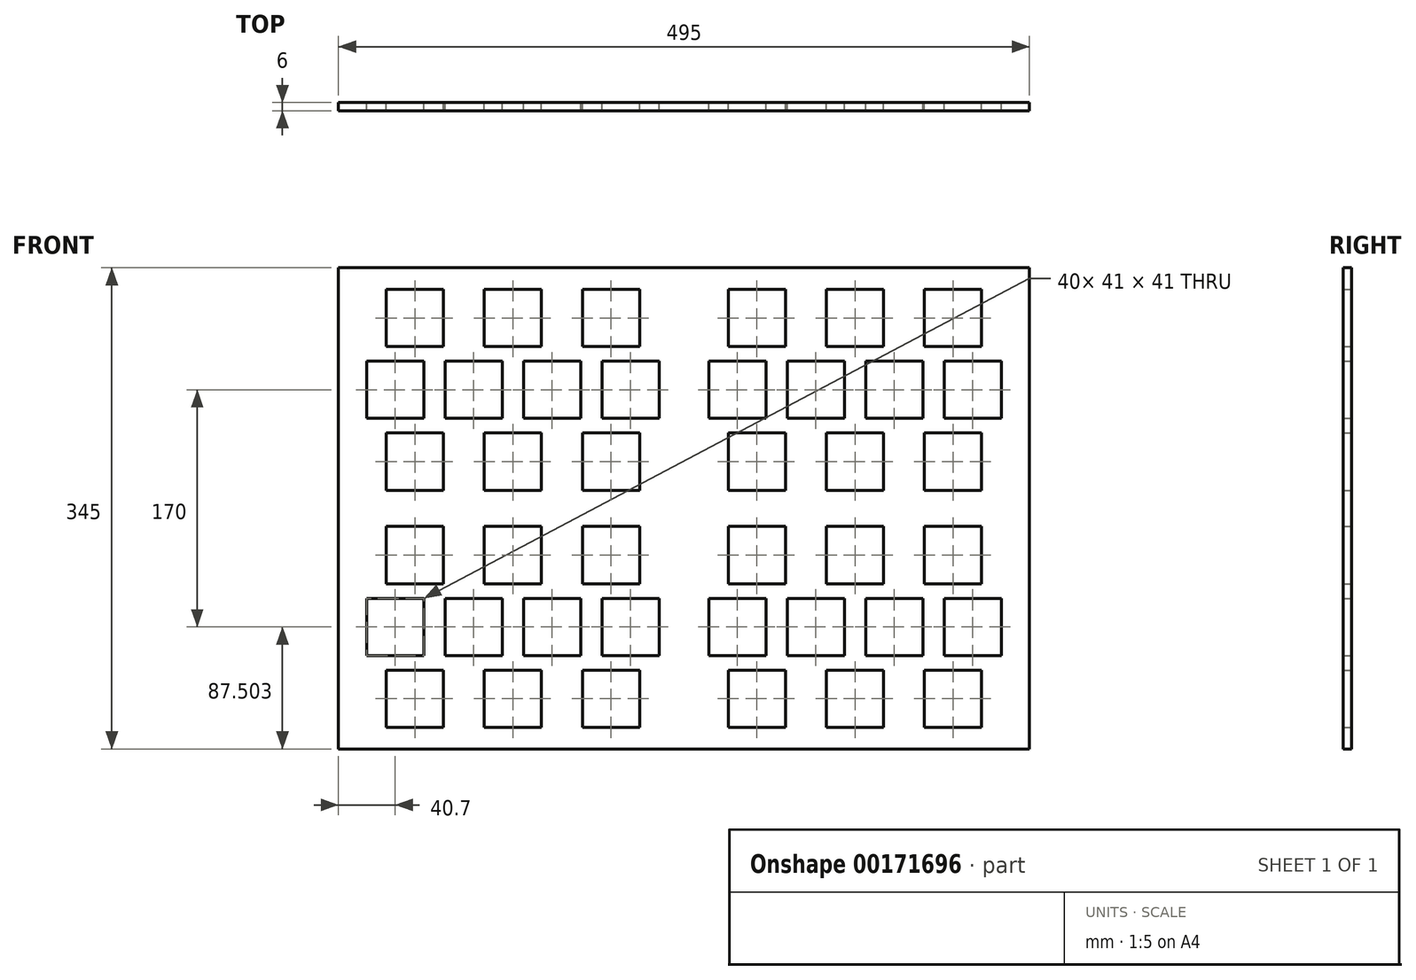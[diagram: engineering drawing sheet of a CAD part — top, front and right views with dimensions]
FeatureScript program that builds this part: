
annotation { "Feature Type Name" : "Feature", "Feature Type Description" : "" }
export const myFeature = defineFeature(function(context is Context, id is Id, definition is map)
    precondition{}
    {
        {
            var Q0;
            Q0=qCreatedBy(makeId("Front.planeOp"),FACE);
            var sketch = newSketch(context, id + "F0", { "sketchPlane" : qUnion([Q0])});
            skLineSegment(sketch, "E0.bottom", {"start": v(228.25, -174.12) * mm, "end": v(-226.75, -174.12) * mm});
            skLineSegment(sketch, "E0.top", {"start": v(227.5, 170.88) * mm, "end": v(-227.5, 170.88) * mm});
            skLineSegment(sketch, "E0.left", {"start": v(248.25, -154.12) * mm, "end": v(248.25, 150.88) * mm});
            skLineSegment(sketch, "E0.right", {"start": v(-246.75, -152.5) * mm, "end": v(-246.75, 152.5) * mm});
            skPoint(sketch, "E1.visualSharp", {"position": v(-246.75, 170.88) * mm});
            skPoint(sketch, "E2.visualSharp", {"position": v(248.25, -174.12) * mm});
            skPoint(sketch, "E3.visualSharp", {"position": v(-246.75, -174.12) * mm});
            skLineSegment(sketch, "E4", {"start": v(-246.75, 152.5) * mm, "end": v(-246.75, 170.88) * mm});
            skLineSegment(sketch, "E5", {"start": v(-246.75, 170.88) * mm, "end": v(-227.5, 170.88) * mm});
            skLineSegment(sketch, "E6", {"start": v(-246.75, -174.12) * mm, "end": v(-246.75, -152.5) * mm});
            skLineSegment(sketch, "E7", {"start": v(-246.75, -174.12) * mm, "end": v(-226.75, -174.12) * mm});
            skLineSegment(sketch, "E8", {"start": v(248.25, -154.12) * mm, "end": v(248.25, -174.12) * mm});
            skLineSegment(sketch, "E9", {"start": v(228.25, -174.12) * mm, "end": v(248.25, -174.12) * mm});
            skLineSegment(sketch, "E10", {"start": v(227.5, 170.88) * mm, "end": v(248.25, 170.88) * mm});
            skLineSegment(sketch, "E11", {"start": v(248.25, 150.88) * mm, "end": v(248.25, 170.88) * mm});
            skPoint(sketch, "E12.0.1.2", {"position": v(-247.5, 2.5) * mm});
            skLineSegment(sketch, "E13.bottom", {"start": v(-212.5, 155.38) * mm, "end": v(-171.5, 155.38) * mm});
            skLineSegment(sketch, "E13.top", {"start": v(-212.5, 114.38) * mm, "end": v(-171.5, 114.38) * mm});
            skLineSegment(sketch, "E13.left", {"start": v(-212.5, 155.38) * mm, "end": v(-212.5, 114.38) * mm});
            skLineSegment(sketch, "E13.right", {"start": v(-171.5, 155.38) * mm, "end": v(-171.5, 114.38) * mm});
            skLineSegment(sketch, "E14.0.1.0", {"start": v(-212.5, 52.38) * mm, "end": v(-171.5, 52.38) * mm});
            skLineSegment(sketch, "E14.0.1.1", {"start": v(-212.5, 11.38) * mm, "end": v(-171.5, 11.38) * mm});
            skLineSegment(sketch, "E14.0.1.2", {"start": v(-171.5, 52.38) * mm, "end": v(-171.5, 11.38) * mm});
            skLineSegment(sketch, "E14.0.1.3", {"start": v(-212.5, 52.38) * mm, "end": v(-212.5, 11.38) * mm});
            skLineSegment(sketch, "E14.1.0.0", {"start": v(-142.25, 155.38) * mm, "end": v(-101.25, 155.38) * mm});
            skLineSegment(sketch, "E14.1.0.1", {"start": v(-142.25, 114.38) * mm, "end": v(-101.25, 114.38) * mm});
            skLineSegment(sketch, "E14.1.0.2", {"start": v(-101.25, 155.38) * mm, "end": v(-101.25, 114.38) * mm});
            skLineSegment(sketch, "E14.1.0.3", {"start": v(-142.25, 155.38) * mm, "end": v(-142.25, 114.38) * mm});
            skLineSegment(sketch, "E14.1.1.0", {"start": v(-142.25, 52.38) * mm, "end": v(-101.25, 52.38) * mm});
            skLineSegment(sketch, "E14.1.1.1", {"start": v(-142.25, 11.38) * mm, "end": v(-101.25, 11.38) * mm});
            skLineSegment(sketch, "E14.1.1.2", {"start": v(-101.25, 52.38) * mm, "end": v(-101.25, 11.38) * mm});
            skLineSegment(sketch, "E14.1.1.3", {"start": v(-142.25, 52.38) * mm, "end": v(-142.25, 11.38) * mm});
            skLineSegment(sketch, "E14.2.0.0", {"start": v(-72, 155.38) * mm, "end": v(-31, 155.38) * mm});
            skLineSegment(sketch, "E14.2.0.1", {"start": v(-72, 114.38) * mm, "end": v(-31, 114.38) * mm});
            skLineSegment(sketch, "E14.2.0.2", {"start": v(-31, 155.38) * mm, "end": v(-31, 114.38) * mm});
            skLineSegment(sketch, "E14.2.0.3", {"start": v(-72, 155.38) * mm, "end": v(-72, 114.38) * mm});
            skLineSegment(sketch, "E14.2.1.0", {"start": v(-72, 52.38) * mm, "end": v(-31, 52.38) * mm});
            skLineSegment(sketch, "E14.2.1.1", {"start": v(-72, 11.38) * mm, "end": v(-31, 11.38) * mm});
            skLineSegment(sketch, "E14.2.1.2", {"start": v(-31, 52.38) * mm, "end": v(-31, 11.38) * mm});
            skLineSegment(sketch, "E14.2.1.3", {"start": v(-72, 52.38) * mm, "end": v(-72, 11.38) * mm});
            skLineSegment(sketch, "E14.direction1", {"start": v(-212.5, 114.38) * mm, "end": v(-142.25, 114.38) * mm, "construction": true});
            skLineSegment(sketch, "E14.direction2", {"start": v(-212.5, 114.38) * mm, "end": v(-212.5, 11.38) * mm, "construction": true});
            skLineSegment(sketch, "E15.bottom", {"start": v(-226.55, 103.88) * mm, "end": v(-185.55, 103.88) * mm});
            skLineSegment(sketch, "E15.top", {"start": v(-226.55, 62.88) * mm, "end": v(-185.55, 62.88) * mm});
            skLineSegment(sketch, "E15.left", {"start": v(-226.55, 103.88) * mm, "end": v(-226.55, 62.88) * mm});
            skLineSegment(sketch, "E15.right", {"start": v(-185.55, 103.88) * mm, "end": v(-185.55, 62.88) * mm});
            skLineSegment(sketch, "E16.1.0.0", {"start": v(-170.35, 103.88) * mm, "end": v(-129.35, 103.88) * mm});
            skLineSegment(sketch, "E16.1.0.1", {"start": v(-129.35, 103.88) * mm, "end": v(-129.35, 62.88) * mm});
            skLineSegment(sketch, "E16.1.0.2", {"start": v(-170.35, 103.88) * mm, "end": v(-170.35, 62.88) * mm});
            skLineSegment(sketch, "E16.1.0.3", {"start": v(-170.35, 62.88) * mm, "end": v(-129.35, 62.88) * mm});
            skLineSegment(sketch, "E16.2.0.0", {"start": v(-114.15, 103.88) * mm, "end": v(-73.15, 103.88) * mm});
            skLineSegment(sketch, "E16.2.0.1", {"start": v(-73.15, 103.88) * mm, "end": v(-73.15, 62.88) * mm});
            skLineSegment(sketch, "E16.2.0.2", {"start": v(-114.15, 103.88) * mm, "end": v(-114.15, 62.88) * mm});
            skLineSegment(sketch, "E16.2.0.3", {"start": v(-114.15, 62.88) * mm, "end": v(-73.15, 62.88) * mm});
            skLineSegment(sketch, "E16.3.0.0", {"start": v(-57.95, 103.88) * mm, "end": v(-16.95, 103.88) * mm});
            skLineSegment(sketch, "E16.3.0.1", {"start": v(-16.95, 103.88) * mm, "end": v(-16.95, 62.88) * mm});
            skLineSegment(sketch, "E16.3.0.2", {"start": v(-57.95, 103.88) * mm, "end": v(-57.95, 62.88) * mm});
            skLineSegment(sketch, "E16.3.0.3", {"start": v(-57.95, 62.88) * mm, "end": v(-16.95, 62.88) * mm});
            skLineSegment(sketch, "E16.direction1", {"start": v(-226.55, 62.88) * mm, "end": v(-170.35, 62.88) * mm, "construction": true});
            skLineSegment(sketch, "E17.0.1.0", {"start": v(-57.95, -107.12) * mm, "end": v(-16.95, -107.12) * mm});
            skLineSegment(sketch, "E17.0.1.1", {"start": v(-72, -14.62) * mm, "end": v(-72, -55.62) * mm});
            skLineSegment(sketch, "E17.0.1.2", {"start": v(-226.55, -66.12) * mm, "end": v(-226.55, -107.12) * mm});
            skLineSegment(sketch, "E17.0.1.3", {"start": v(-185.55, -66.12) * mm, "end": v(-185.55, -107.12) * mm});
            skLineSegment(sketch, "E17.0.1.4", {"start": v(-72, -55.62) * mm, "end": v(-31, -55.62) * mm});
            skLineSegment(sketch, "E17.0.1.5", {"start": v(-57.95, -66.12) * mm, "end": v(-57.95, -107.12) * mm});
            skLineSegment(sketch, "E17.0.1.6", {"start": v(-170.35, -66.12) * mm, "end": v(-129.35, -66.12) * mm});
            skLineSegment(sketch, "E17.0.1.7", {"start": v(-212.5, -117.62) * mm, "end": v(-171.5, -117.62) * mm});
            skLineSegment(sketch, "E17.0.1.8", {"start": v(-212.5, -158.62) * mm, "end": v(-171.5, -158.62) * mm});
            skLineSegment(sketch, "E17.0.1.9", {"start": v(-73.15, -66.12) * mm, "end": v(-73.15, -107.12) * mm});
            skLineSegment(sketch, "E17.0.1.10", {"start": v(-114.15, -66.12) * mm, "end": v(-114.15, -107.12) * mm});
            skLineSegment(sketch, "E17.0.1.11", {"start": v(-72, -117.62) * mm, "end": v(-31, -117.62) * mm});
            skLineSegment(sketch, "E17.0.1.12", {"start": v(-72, -158.62) * mm, "end": v(-31, -158.62) * mm});
            skLineSegment(sketch, "E17.0.1.13", {"start": v(-212.5, -14.62) * mm, "end": v(-171.5, -14.62) * mm});
            skLineSegment(sketch, "E17.0.1.14", {"start": v(-226.55, -107.12) * mm, "end": v(-170.35, -107.12) * mm, "construction": true});
            skLineSegment(sketch, "E17.0.1.15", {"start": v(-31, -117.62) * mm, "end": v(-31, -158.62) * mm});
            skLineSegment(sketch, "E17.0.1.16", {"start": v(-142.25, -117.62) * mm, "end": v(-142.25, -158.62) * mm});
            skLineSegment(sketch, "E17.0.1.17", {"start": v(-129.35, -66.12) * mm, "end": v(-129.35, -107.12) * mm});
            skLineSegment(sketch, "E17.0.1.18", {"start": v(-57.95, -66.12) * mm, "end": v(-16.95, -66.12) * mm});
            skLineSegment(sketch, "E17.0.1.19", {"start": v(-170.35, -66.12) * mm, "end": v(-170.35, -107.12) * mm});
            skLineSegment(sketch, "E17.0.1.20", {"start": v(-114.15, -107.12) * mm, "end": v(-73.15, -107.12) * mm});
            skLineSegment(sketch, "E17.0.1.21", {"start": v(-142.25, -55.62) * mm, "end": v(-101.25, -55.62) * mm});
            skLineSegment(sketch, "E17.0.1.22", {"start": v(-212.5, -55.62) * mm, "end": v(-212.5, -158.62) * mm, "construction": true});
            skLineSegment(sketch, "E17.0.1.23", {"start": v(-72, -14.62) * mm, "end": v(-31, -14.62) * mm});
            skLineSegment(sketch, "E17.0.1.24", {"start": v(-16.95, -66.12) * mm, "end": v(-16.95, -107.12) * mm});
            skLineSegment(sketch, "E17.0.1.25", {"start": v(-72, -117.62) * mm, "end": v(-72, -158.62) * mm});
            skLineSegment(sketch, "E17.0.1.26", {"start": v(-171.5, -14.62) * mm, "end": v(-171.5, -55.62) * mm});
            skLineSegment(sketch, "E17.0.1.27", {"start": v(-142.25, -117.62) * mm, "end": v(-101.25, -117.62) * mm});
            skLineSegment(sketch, "E17.0.1.28", {"start": v(-226.55, -66.12) * mm, "end": v(-185.55, -66.12) * mm});
            skLineSegment(sketch, "E17.0.1.29", {"start": v(-101.25, -117.62) * mm, "end": v(-101.25, -158.62) * mm});
            skLineSegment(sketch, "E17.0.1.30", {"start": v(-114.15, -66.12) * mm, "end": v(-73.15, -66.12) * mm});
            skLineSegment(sketch, "E17.0.1.31", {"start": v(-31, -14.62) * mm, "end": v(-31, -55.62) * mm});
            skLineSegment(sketch, "E17.0.1.32", {"start": v(-212.5, -14.62) * mm, "end": v(-212.5, -55.62) * mm});
            skLineSegment(sketch, "E17.0.1.33", {"start": v(-142.25, -158.62) * mm, "end": v(-101.25, -158.62) * mm});
            skLineSegment(sketch, "E17.0.1.34", {"start": v(-212.5, -55.62) * mm, "end": v(-142.25, -55.62) * mm, "construction": true});
            skLineSegment(sketch, "E17.0.1.35", {"start": v(-142.25, -14.62) * mm, "end": v(-142.25, -55.62) * mm});
            skLineSegment(sketch, "E17.0.1.36", {"start": v(-170.35, -107.12) * mm, "end": v(-129.35, -107.12) * mm});
            skLineSegment(sketch, "E17.0.1.37", {"start": v(-171.5, -117.62) * mm, "end": v(-171.5, -158.62) * mm});
            skLineSegment(sketch, "E17.0.1.38", {"start": v(-101.25, -14.62) * mm, "end": v(-101.25, -55.62) * mm});
            skLineSegment(sketch, "E17.0.1.39", {"start": v(-142.25, -14.62) * mm, "end": v(-101.25, -14.62) * mm});
            skLineSegment(sketch, "E17.0.1.40", {"start": v(-212.5, -55.62) * mm, "end": v(-171.5, -55.62) * mm});
            skLineSegment(sketch, "E17.0.1.41", {"start": v(-226.55, -107.12) * mm, "end": v(-185.55, -107.12) * mm});
            skLineSegment(sketch, "E17.0.1.42", {"start": v(-212.5, -117.62) * mm, "end": v(-212.5, -158.62) * mm});
            skLineSegment(sketch, "E17.1.0.0", {"start": v(187.05, 62.88) * mm, "end": v(228.05, 62.88) * mm});
            skLineSegment(sketch, "E17.1.0.1", {"start": v(173, 155.38) * mm, "end": v(173, 114.38) * mm});
            skLineSegment(sketch, "E17.1.0.2", {"start": v(18.45, 103.88) * mm, "end": v(18.45, 62.88) * mm});
            skLineSegment(sketch, "E17.1.0.3", {"start": v(59.45, 103.88) * mm, "end": v(59.45, 62.88) * mm});
            skLineSegment(sketch, "E17.1.0.4", {"start": v(173, 114.38) * mm, "end": v(214, 114.38) * mm});
            skLineSegment(sketch, "E17.1.0.5", {"start": v(187.05, 103.88) * mm, "end": v(187.05, 62.88) * mm});
            skLineSegment(sketch, "E17.1.0.6", {"start": v(74.65, 103.88) * mm, "end": v(115.65, 103.88) * mm});
            skLineSegment(sketch, "E17.1.0.7", {"start": v(32.5, 52.38) * mm, "end": v(73.5, 52.38) * mm});
            skLineSegment(sketch, "E17.1.0.8", {"start": v(32.5, 11.38) * mm, "end": v(73.5, 11.38) * mm});
            skLineSegment(sketch, "E17.1.0.9", {"start": v(171.85, 103.88) * mm, "end": v(171.85, 62.88) * mm});
            skLineSegment(sketch, "E17.1.0.10", {"start": v(130.85, 103.88) * mm, "end": v(130.85, 62.88) * mm});
            skLineSegment(sketch, "E17.1.0.11", {"start": v(173, 52.38) * mm, "end": v(214, 52.38) * mm});
            skLineSegment(sketch, "E17.1.0.12", {"start": v(173, 11.38) * mm, "end": v(214, 11.38) * mm});
            skLineSegment(sketch, "E17.1.0.13", {"start": v(32.5, 155.38) * mm, "end": v(73.5, 155.38) * mm});
            skLineSegment(sketch, "E17.1.0.14", {"start": v(18.45, 62.88) * mm, "end": v(74.65, 62.88) * mm, "construction": true});
            skLineSegment(sketch, "E17.1.0.15", {"start": v(214, 52.38) * mm, "end": v(214, 11.38) * mm});
            skLineSegment(sketch, "E17.1.0.16", {"start": v(102.75, 52.38) * mm, "end": v(102.75, 11.38) * mm});
            skLineSegment(sketch, "E17.1.0.17", {"start": v(115.65, 103.88) * mm, "end": v(115.65, 62.88) * mm});
            skLineSegment(sketch, "E17.1.0.18", {"start": v(187.05, 103.88) * mm, "end": v(228.05, 103.88) * mm});
            skLineSegment(sketch, "E17.1.0.19", {"start": v(74.65, 103.88) * mm, "end": v(74.65, 62.88) * mm});
            skLineSegment(sketch, "E17.1.0.20", {"start": v(130.85, 62.88) * mm, "end": v(171.85, 62.88) * mm});
            skLineSegment(sketch, "E17.1.0.21", {"start": v(102.75, 114.38) * mm, "end": v(143.75, 114.38) * mm});
            skLineSegment(sketch, "E17.1.0.22", {"start": v(32.5, 114.38) * mm, "end": v(32.5, 11.38) * mm, "construction": true});
            skLineSegment(sketch, "E17.1.0.23", {"start": v(173, 155.38) * mm, "end": v(214, 155.38) * mm});
            skLineSegment(sketch, "E17.1.0.24", {"start": v(228.05, 103.88) * mm, "end": v(228.05, 62.88) * mm});
            skLineSegment(sketch, "E17.1.0.25", {"start": v(173, 52.38) * mm, "end": v(173, 11.38) * mm});
            skLineSegment(sketch, "E17.1.0.26", {"start": v(73.5, 155.38) * mm, "end": v(73.5, 114.38) * mm});
            skLineSegment(sketch, "E17.1.0.27", {"start": v(102.75, 52.38) * mm, "end": v(143.75, 52.38) * mm});
            skLineSegment(sketch, "E17.1.0.28", {"start": v(18.45, 103.88) * mm, "end": v(59.45, 103.88) * mm});
            skLineSegment(sketch, "E17.1.0.29", {"start": v(143.75, 52.38) * mm, "end": v(143.75, 11.38) * mm});
            skLineSegment(sketch, "E17.1.0.30", {"start": v(130.85, 103.88) * mm, "end": v(171.85, 103.88) * mm});
            skLineSegment(sketch, "E17.1.0.31", {"start": v(214, 155.38) * mm, "end": v(214, 114.38) * mm});
            skLineSegment(sketch, "E17.1.0.32", {"start": v(32.5, 155.38) * mm, "end": v(32.5, 114.38) * mm});
            skLineSegment(sketch, "E17.1.0.33", {"start": v(102.75, 11.38) * mm, "end": v(143.75, 11.38) * mm});
            skLineSegment(sketch, "E17.1.0.34", {"start": v(32.5, 114.38) * mm, "end": v(102.75, 114.38) * mm, "construction": true});
            skLineSegment(sketch, "E17.1.0.35", {"start": v(102.75, 155.38) * mm, "end": v(102.75, 114.38) * mm});
            skLineSegment(sketch, "E17.1.0.36", {"start": v(74.65, 62.88) * mm, "end": v(115.65, 62.88) * mm});
            skLineSegment(sketch, "E17.1.0.37", {"start": v(73.5, 52.38) * mm, "end": v(73.5, 11.38) * mm});
            skLineSegment(sketch, "E17.1.0.38", {"start": v(143.75, 155.38) * mm, "end": v(143.75, 114.38) * mm});
            skLineSegment(sketch, "E17.1.0.39", {"start": v(102.75, 155.38) * mm, "end": v(143.75, 155.38) * mm});
            skLineSegment(sketch, "E17.1.0.40", {"start": v(32.5, 114.38) * mm, "end": v(73.5, 114.38) * mm});
            skLineSegment(sketch, "E17.1.0.41", {"start": v(18.45, 62.88) * mm, "end": v(59.45, 62.88) * mm});
            skLineSegment(sketch, "E17.1.0.42", {"start": v(32.5, 52.38) * mm, "end": v(32.5, 11.38) * mm});
            skLineSegment(sketch, "E17.1.1.0", {"start": v(187.05, -107.12) * mm, "end": v(228.05, -107.12) * mm});
            skLineSegment(sketch, "E17.1.1.1", {"start": v(173, -14.62) * mm, "end": v(173, -55.62) * mm});
            skLineSegment(sketch, "E17.1.1.2", {"start": v(18.45, -66.12) * mm, "end": v(18.45, -107.12) * mm});
            skLineSegment(sketch, "E17.1.1.3", {"start": v(59.45, -66.12) * mm, "end": v(59.45, -107.12) * mm});
            skLineSegment(sketch, "E17.1.1.4", {"start": v(173, -55.62) * mm, "end": v(214, -55.62) * mm});
            skLineSegment(sketch, "E17.1.1.5", {"start": v(187.05, -66.12) * mm, "end": v(187.05, -107.12) * mm});
            skLineSegment(sketch, "E17.1.1.6", {"start": v(74.65, -66.12) * mm, "end": v(115.65, -66.12) * mm});
            skLineSegment(sketch, "E17.1.1.7", {"start": v(32.5, -117.62) * mm, "end": v(73.5, -117.62) * mm});
            skLineSegment(sketch, "E17.1.1.8", {"start": v(32.5, -158.62) * mm, "end": v(73.5, -158.62) * mm});
            skLineSegment(sketch, "E17.1.1.9", {"start": v(171.85, -66.12) * mm, "end": v(171.85, -107.12) * mm});
            skLineSegment(sketch, "E17.1.1.10", {"start": v(130.85, -66.12) * mm, "end": v(130.85, -107.12) * mm});
            skLineSegment(sketch, "E17.1.1.11", {"start": v(173, -117.62) * mm, "end": v(214, -117.62) * mm});
            skLineSegment(sketch, "E17.1.1.12", {"start": v(173, -158.62) * mm, "end": v(214, -158.62) * mm});
            skLineSegment(sketch, "E17.1.1.13", {"start": v(32.5, -14.62) * mm, "end": v(73.5, -14.62) * mm});
            skLineSegment(sketch, "E17.1.1.14", {"start": v(18.45, -107.12) * mm, "end": v(74.65, -107.12) * mm, "construction": true});
            skLineSegment(sketch, "E17.1.1.15", {"start": v(214, -117.62) * mm, "end": v(214, -158.62) * mm});
            skLineSegment(sketch, "E17.1.1.16", {"start": v(102.75, -117.62) * mm, "end": v(102.75, -158.62) * mm});
            skLineSegment(sketch, "E17.1.1.17", {"start": v(115.65, -66.12) * mm, "end": v(115.65, -107.12) * mm});
            skLineSegment(sketch, "E17.1.1.18", {"start": v(187.05, -66.12) * mm, "end": v(228.05, -66.12) * mm});
            skLineSegment(sketch, "E17.1.1.19", {"start": v(74.65, -66.12) * mm, "end": v(74.65, -107.12) * mm});
            skLineSegment(sketch, "E17.1.1.20", {"start": v(130.85, -107.12) * mm, "end": v(171.85, -107.12) * mm});
            skLineSegment(sketch, "E17.1.1.21", {"start": v(102.75, -55.62) * mm, "end": v(143.75, -55.62) * mm});
            skLineSegment(sketch, "E17.1.1.22", {"start": v(32.5, -55.62) * mm, "end": v(32.5, -158.62) * mm, "construction": true});
            skLineSegment(sketch, "E17.1.1.23", {"start": v(173, -14.62) * mm, "end": v(214, -14.62) * mm});
            skLineSegment(sketch, "E17.1.1.24", {"start": v(228.05, -66.12) * mm, "end": v(228.05, -107.12) * mm});
            skLineSegment(sketch, "E17.1.1.25", {"start": v(173, -117.62) * mm, "end": v(173, -158.62) * mm});
            skLineSegment(sketch, "E17.1.1.26", {"start": v(73.5, -14.62) * mm, "end": v(73.5, -55.62) * mm});
            skLineSegment(sketch, "E17.1.1.27", {"start": v(102.75, -117.62) * mm, "end": v(143.75, -117.62) * mm});
            skLineSegment(sketch, "E17.1.1.28", {"start": v(18.45, -66.12) * mm, "end": v(59.45, -66.12) * mm});
            skLineSegment(sketch, "E17.1.1.29", {"start": v(143.75, -117.62) * mm, "end": v(143.75, -158.62) * mm});
            skLineSegment(sketch, "E17.1.1.30", {"start": v(130.85, -66.12) * mm, "end": v(171.85, -66.12) * mm});
            skLineSegment(sketch, "E17.1.1.31", {"start": v(214, -14.62) * mm, "end": v(214, -55.62) * mm});
            skLineSegment(sketch, "E17.1.1.32", {"start": v(32.5, -14.62) * mm, "end": v(32.5, -55.62) * mm});
            skLineSegment(sketch, "E17.1.1.33", {"start": v(102.75, -158.62) * mm, "end": v(143.75, -158.62) * mm});
            skLineSegment(sketch, "E17.1.1.34", {"start": v(32.5, -55.62) * mm, "end": v(102.75, -55.62) * mm, "construction": true});
            skLineSegment(sketch, "E17.1.1.35", {"start": v(102.75, -14.62) * mm, "end": v(102.75, -55.62) * mm});
            skLineSegment(sketch, "E17.1.1.36", {"start": v(74.65, -107.12) * mm, "end": v(115.65, -107.12) * mm});
            skLineSegment(sketch, "E17.1.1.37", {"start": v(73.5, -117.62) * mm, "end": v(73.5, -158.62) * mm});
            skLineSegment(sketch, "E17.1.1.38", {"start": v(143.75, -14.62) * mm, "end": v(143.75, -55.62) * mm});
            skLineSegment(sketch, "E17.1.1.39", {"start": v(102.75, -14.62) * mm, "end": v(143.75, -14.62) * mm});
            skLineSegment(sketch, "E17.1.1.40", {"start": v(32.5, -55.62) * mm, "end": v(73.5, -55.62) * mm});
            skLineSegment(sketch, "E17.1.1.41", {"start": v(18.45, -107.12) * mm, "end": v(59.45, -107.12) * mm});
            skLineSegment(sketch, "E17.1.1.42", {"start": v(32.5, -117.62) * mm, "end": v(32.5, -158.62) * mm});
            skLineSegment(sketch, "E17.direction1", {"start": v(-212.5, 11.38) * mm, "end": v(32.5, 11.38) * mm, "construction": true});
            skLineSegment(sketch, "E17.direction2", {"start": v(-212.5, 11.38) * mm, "end": v(-212.5, -158.62) * mm, "construction": true});
            skSolve(sketch);
        }
        {
            var Q0;
            Q0=qSketchRegion(id+"F0",true);
            extrude(context, id + "F1", {"entities" : qUnion([Q0]), "depth" : 6 * mm, "offsetDistance" : 25 * mm});
        }
    });
